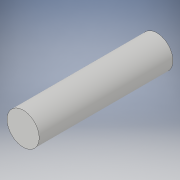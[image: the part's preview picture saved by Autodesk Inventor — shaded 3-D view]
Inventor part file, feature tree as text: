
AUTODESK INVENTOR PART (.ipt)
format: ipt  version: 2019 (Build 230136000, 136)  size: 89,088 bytes
history: native  units: mm
features: extrude x1, sketch x1
ambient origin geometry x8: Origin, YZ Plane, XZ Plane, XY Plane, X Axis, Y Axis, Z Axis, Center Point
bodies: Solid1 (feature_tree)
feature tree (2):
  extrude  "Extrusion1"  Depth=20.0mm TaperAngle=0.0deg
  sketch  "Sketch1"  dims[d0=4.8mm d1=20.0mm d2=0.0mm]
